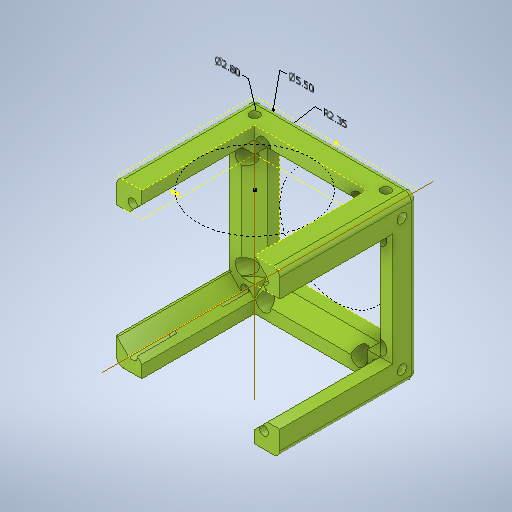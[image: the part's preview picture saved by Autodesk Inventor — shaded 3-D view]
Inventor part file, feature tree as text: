
AUTODESK INVENTOR PART (.ipt)
format: ipt  version: 2025.1 (Build 291241000, 241)  size: 652,800 bytes
history: native  units: mm
features: sketch x15, projected_geometry x10, hole x7, extrude x6, other x5, plane x2, fillet x1
ambient origin geometry x8: Origin, YZ Plane, XZ Plane, XY Plane, X Axis, Y Axis, Z Axis, Center Point
bodies: Solid1 (feature_tree)
feature tree (46):
  extrude  "Extrusion1"  Depth=49.8mm
  extrude  "Extrusion2"  Depth=7.7mm TaperAngle=0.0deg
  hole  "Hole1"  [1 undecoded]
  sketch  "Sketch4"  dims[d8=2.8mm d9=6.0mm d10=5.5mm d11=3.1mm d12=90.0deg d13=16.0mm d14=20.594885mm d23=2.0mm d30=33.8mm d31=0.0mm]
  sketch  "Sketch5"  dims[d35=33.8mm d36=0.0mm d37=54.2mm]
  other  "Work Axis1"
  other  "Work Axis2"
  fillet  "Fillet1"  Radius=33.8mm
  extrude  "Extrusion3"  Depth=54.2mm
  extrude  "Extrusion4"  Depth=54.2mm
  plane  "Work Plane1"
  extrude  "Extrusion5"  Depth=4.9mm
  hole  "Hole2"  [1 undecoded]
  hole  "Hole4"  [1 undecoded]
  hole  "Hole5"  [1 undecoded]
  hole  "Hole6"  [1 undecoded]
  hole  "Hole7"  [1 undecoded]
  hole  "Hole8"  [1 undecoded]
  sketch  "草图16"  dims[d81=2.9mm d82=6.0mm d83=4.0mm d84=2.0mm d85=90.0deg d86=6.5mm d87=20.594885mm d88=4.9mm]
  sketch  "草图17"  dims[d89=4.9mm d90=4.9mm]
  plane  "工作平面2"
  extrude  "拉伸6"  Depth=5.0mm
  sketch  "草图19"  dims[d93=4.9mm d94=4.9mm d96=4.9mm d97=4.9mm d98=4.9mm d99=4.9mm d100=4.9mm d101=4.9mm d102=4.9mm d111=0.0mm d113=4.7mm d114=6.0mm d115=4.0mm d116=2.0mm d117=90.0deg d118=8.0mm d119=20.594885mm d120=54.2mm d121=54.2mm d122=54.0mm d123=54.0mm d124=5.0mm d125=0.0mm d126=12.649154mm d127=2.8mm d128=11.211842mm d129=5.5mm d130=7.016027mm d131=2.35mm]
  sketch  "Sketch1"  dims[d0=49.8mm d1=49.8mm]
  sketch  "Sketch2"  dims[d2=7.7mm d3=7.7mm d4=0.0mm]
  projected_geometry  "Projected Loop1"
  sketch  "Sketch3"  dims[d5=34.4mm d6=0.0mm]
  projected_geometry  "Projected Loop3"
  projected_geometry  "Projected Loop4"
  projected_geometry  "Projected Loop5"
  projected_geometry  "Projected Loop6"
  projected_geometry  "Projected Loop7"
  sketch  "Sketch9"  dims[d38=135.0deg d39=54.2mm]
  sketch  "Sketch11"  dims[d40=33.8mm d41=0.0mm]
  projected_geometry  "Projected Loop11"
  sketch  "Sketch12"  dims[d42=2.8mm d43=6.0mm d44=3.0mm d45=2.0mm d46=90.0deg d47=12.0mm d48=20.594885mm]
  sketch  "Sketch13"  dims[d58=2.9mm d59=6.0mm d60=4.0mm d61=2.0mm d62=90.0deg d63=6.5mm d64=20.594885mm]
  sketch  "Sketch14"  dims[d67=2.9mm d68=6.0mm d69=4.0mm d70=2.0mm d71=90.0deg d72=6.5mm d73=20.594885mm]
  sketch  "Sketch15"  dims[d74=2.9mm d75=6.0mm d76=4.0mm d77=2.0mm d78=90.0deg d79=6.5mm d80=20.594885mm]
  projected_geometry  "Projected Loop13"
  projected_geometry  "Projected Loop14"
  projected_geometry  "投影回路15"
  sketch  "草图18"  dims[d91=4.9mm d92=4.9mm]
  other  "直径尺寸 1"
  other  "直径尺寸 2"
  other  "半径尺寸 1"
note: 7 required parameter values undecoded (feature->parameter linkage not recoverable at this tier; creation-order binding heuristic only, values carry confidence <= 0.55)
